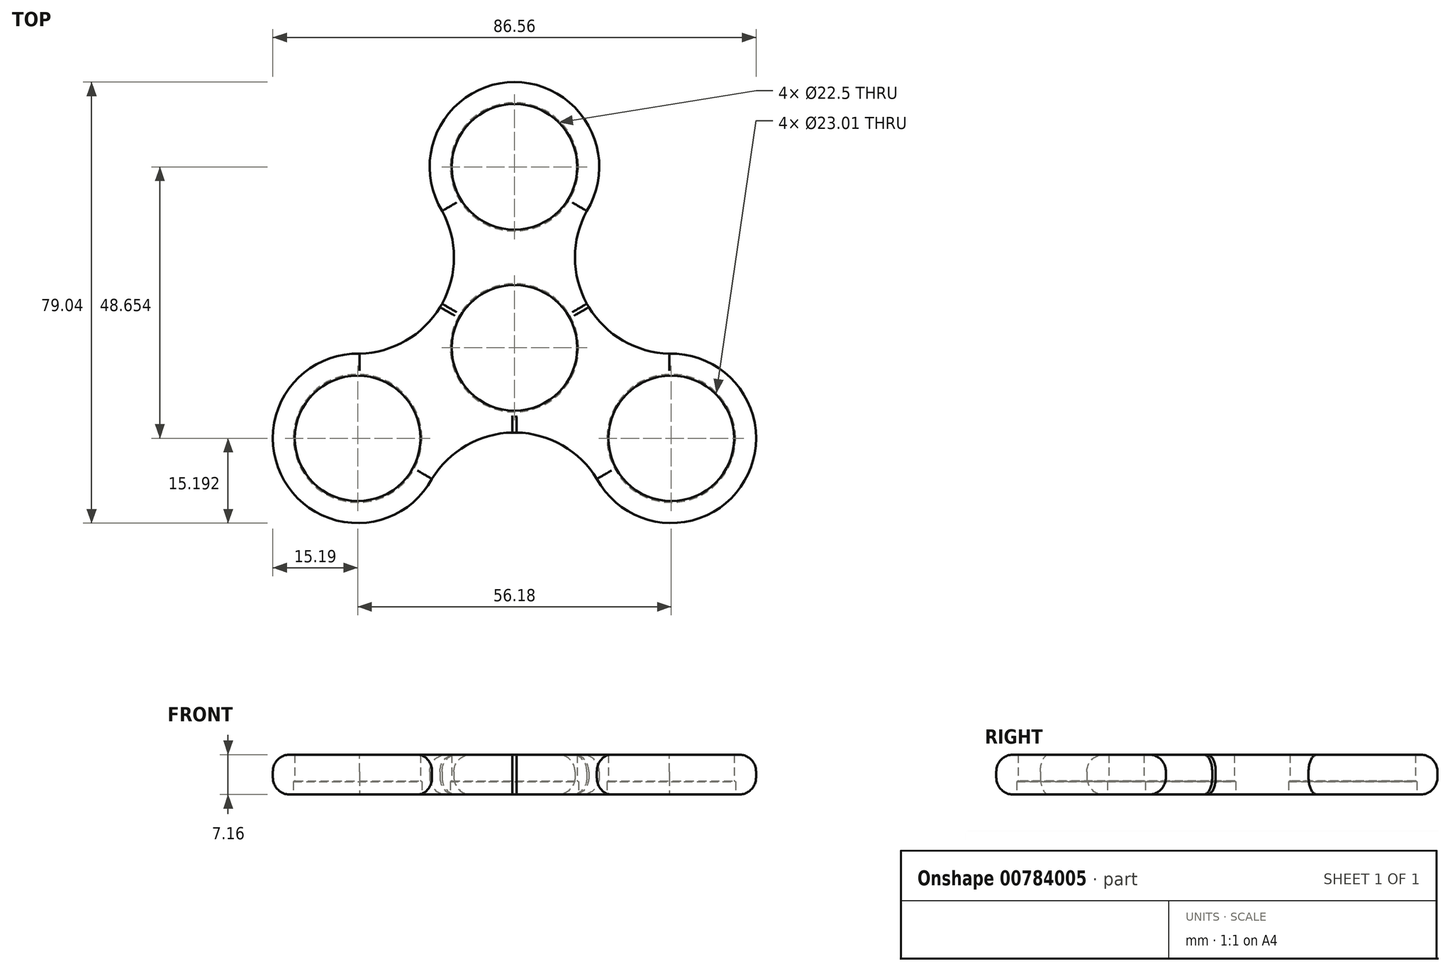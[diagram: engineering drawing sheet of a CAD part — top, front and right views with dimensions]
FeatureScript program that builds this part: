
annotation { "Feature Type Name" : "Feature", "Feature Type Description" : "" }
export const myFeature = defineFeature(function(context is Context, id is Id, definition is map)
    precondition{}
    {
        {
            var Q0;
            Q0=qCreatedBy(makeId("Top.planeOp"),FACE);
            var sketch = newSketch(context, id + "F0", { "sketchPlane" : qUnion([Q0])});
            skCircle(sketch, "E0", {"center": v(0, 0) * mm, "radius": 11.25 * mm});
            skCircle(sketch, "E1", {"center": v(0, 0) * mm, "radius": 15.19 * mm});
            skCircle(sketch, "E2.1.0", {"center": v(0, 32.44) * mm, "radius": 15.19 * mm});
            skCircle(sketch, "E2.1.1", {"center": v(0, 32.44) * mm, "radius": 11.25 * mm});
            skLineSegment(sketch, "E3", {"start": v(0, 0) * mm, "end": v(0, 32.44) * mm, "construction": true});
            skLineSegment(sketch, "E4", {"start": v(0, 32.44) * mm, "end": v(28.1, 16.22) * mm, "construction": true});
            skArc(sketch, "E5", {"start": v(13.33, 7.28) * mm, "mid": v(10.84, 16.04) * mm, "end": v(13.15, 24.85) * mm});
            skArc(sketch, "E6.MirrorCS", {"start": v(-13.33, 7.28) * mm, "mid": v(-10.84, 16.04) * mm, "end": v(-13.15, 24.85) * mm});
            skCircle(sketch, "E7.1.1", {"center": v(-28.1, -16.22) * mm, "radius": 11.25 * mm});
            skCircle(sketch, "E7.1.2", {"center": v(-28.1, -16.22) * mm, "radius": 15.19 * mm});
            skArc(sketch, "E7.1.3", {"start": v(0.36, -15.18) * mm, "mid": v(-8.47, -17.4) * mm, "end": v(-14.94, -23.8) * mm});
            skArc(sketch, "E7.1.4", {"start": v(-12.97, 7.9) * mm, "mid": v(-19.3, 1.37) * mm, "end": v(-28.1, -1.04) * mm});
            skCircle(sketch, "E7.2.1", {"center": v(28.1, -16.22) * mm, "radius": 11.25 * mm});
            skCircle(sketch, "E7.2.2", {"center": v(28.1, -16.22) * mm, "radius": 15.19 * mm});
            skArc(sketch, "E7.2.3", {"start": v(12.97, 7.9) * mm, "mid": v(19.3, 1.37) * mm, "end": v(28.1, -1.04) * mm});
            skArc(sketch, "E7.2.4", {"start": v(-0.36, -15.18) * mm, "mid": v(8.47, -17.4) * mm, "end": v(14.94, -23.8) * mm});
            skSolve(sketch);
        }
        {
            var Q0;
            Q0 = qSketchRegion(id + "F0", true);
            extrude(context, id + "F1", {"entities" : qUnion([Q0]), "depth" : 7.16 * mm, "offsetDistance" : 25.4 * mm});
        }
        {
            var Q0;
            Q0=sQuery(id+"F0.wireOp",VERTEX,"E2.1.2.start");
            var Q1;
            Q1=sQuery(id+"F0.wireOp",VERTEX,"E0.center");
            var Q2;
            Q2=sQuery(id+"F0.wireOp",VERTEX,"DuPa364O-TqXS-B9n7-HQNF-Pfb0DS6MvXj8.end");
            var Q3;
            Q3=sQuery(id+"F0.wireOp",VERTEX,"E2.2.2.start");
            var Q4;
            Q4=makeQuery(id+"F1.opExtrude","SWEPT_BODY",BODY,{"disambiguationData":[OSD([sQuery(id+"F0.wireOp",EDGE,"E0"),sQuery(id+"F0.wireOp",EDGE,"49040aab-aefb-4229-aee8-8bc108439dca"),sQuery(id+"F0.wireOp",EDGE,"cf4a4477-fab2-41f1-a485-c14e34cd1196"),sQuery(id+"F0.wireOp",EDGE,"E2.1.0"),sQuery(id+"F0.wireOp",EDGE,"E2.1.1"),sQuery(id+"F0.wireOp",EDGE,"E2.2.0"),sQuery(id+"F0.wireOp",EDGE,"E2.2.1"),sQuery(id+"F0.wireOp",EDGE,"L5vnPDiK-83xg-WwNy-e8JY-2QZKI3Z6EqPW"),sQuery(id+"F0.wireOp",EDGE,"0c184fe2-091d-4b9e-b4e7-c48332455db4.1.0"),sQuery(id+"F0.wireOp",EDGE,"0c184fe2-091d-4b9e-b4e7-c48332455db4.2.0")])]});
            hole(context, id + "F2", {"style" : HoleStyle.SIMPLE, "endStyle" : HoleEndStyle.BLIND, "oppositeDirection" : true, "holeDiameter" : 23.01 * mm, "majorDiameter" : 6.35 * mm, "holeDepth" : 2.3 * mm, "isTappedThrough" : true, "tappedDepth" : 12.7 * mm, "tapClearance" : 3, "locations" : qUnion([Q0, Q1, Q2, Q3]), "scope" : qUnion([Q4])});
        }
        {
            var Q0;
            Q0=sQuery(id+"F0.wireOp",VERTEX,"E7.1.1.center");
            var Q1;
            Q1=sQuery(id+"F0.wireOp",VERTEX,"E7.2.1.center");
            var Q2;
            Q2=sQuery(id+"F0.wireOp",VERTEX,"E3.end");
            var Q3;
            Q3=makeQuery(id+"F1.opExtrude","SWEPT_BODY",BODY,{"disambiguationData":[OSD([sQuery(id+"F0.wireOp",EDGE,"E0"),sQuery(id+"F0.wireOp",EDGE,"E1"),sQuery(id+"F0.wireOp",EDGE,"E2.1.0"),sQuery(id+"F0.wireOp",EDGE,"E2.1.1"),sQuery(id+"F0.wireOp",EDGE,"E5"),sQuery(id+"F0.wireOp",EDGE,"E6.MirrorCS"),sQuery(id+"F0.wireOp",EDGE,"E7.1.1"),sQuery(id+"F0.wireOp",EDGE,"E7.1.2"),sQuery(id+"F0.wireOp",EDGE,"E7.1.3"),sQuery(id+"F0.wireOp",EDGE,"E7.1.4"),sQuery(id+"F0.wireOp",EDGE,"E7.2.1"),sQuery(id+"F0.wireOp",EDGE,"E7.2.2"),sQuery(id+"F0.wireOp",EDGE,"E7.2.3"),sQuery(id+"F0.wireOp",EDGE,"E7.2.4")])]});
            hole(context, id + "F3", {"style" : HoleStyle.SIMPLE, "endStyle" : HoleEndStyle.BLIND, "oppositeDirection" : true, "holeDiameter" : 23.01 * mm, "majorDiameter" : 6.35 * mm, "holeDepth" : 2.3 * mm, "isTappedThrough" : true, "tappedDepth" : 12.7 * mm, "tapClearance" : 3, "locations" : qUnion([Q0, Q1, Q2]), "scope" : qUnion([Q3])});
        }
        {
            var Q0;
            Q0=makeQuery(id+"F1.opExtrude","CAP_EDGE",EDGE,{"disambiguationData":[OSD([sQuery(id+"F0.wireOp",EDGE,"E7.1.4")])],"isStart":false});
            var Q1;
            Q1=makeQuery(id+"F1.opExtrude","CAP_EDGE",EDGE,{"disambiguationData":[OSD([sQuery(id+"F0.wireOp",EDGE,"E7.1.2")])],"isStart":false});
            var Q2;
            Q2=makeQuery(id+"F1.opExtrude","CAP_EDGE",EDGE,{"disambiguationData":[OSD([sQuery(id+"F0.wireOp",EDGE,"E7.1.3")])],"isStart":false});
            var Q3;
            Q3=makeQuery(id+"F1.opExtrude","CAP_EDGE",EDGE,{"disambiguationData":[OSD([sQuery(id+"F0.wireOp",EDGE,"E7.2.4")])],"isStart":false});
            var Q4;
            Q4=makeQuery(id+"F1.opExtrude","CAP_EDGE",EDGE,{"disambiguationData":[OSD([sQuery(id+"F0.wireOp",EDGE,"E7.2.2")])],"isStart":false});
            var Q5;
            Q5=makeQuery(id+"F1.opExtrude","CAP_EDGE",EDGE,{"disambiguationData":[OSD([sQuery(id+"F0.wireOp",EDGE,"E7.2.3")])],"isStart":false});
            var Q6;
            Q6=makeQuery(id+"F1.opExtrude","CAP_EDGE",EDGE,{"disambiguationData":[OSD([sQuery(id+"F0.wireOp",EDGE,"E5")])],"isStart":false});
            var Q7;
            Q7=makeQuery(id+"F1.opExtrude","CAP_EDGE",EDGE,{"disambiguationData":[OSD([sQuery(id+"F0.wireOp",EDGE,"E2.1.0")])],"isStart":false});
            var Q8;
            Q8=makeQuery(id+"F1.opExtrude","CAP_EDGE",EDGE,{"disambiguationData":[OSD([sQuery(id+"F0.wireOp",EDGE,"E6.MirrorCS")])],"isStart":false});
            var Q9;
            {var subQ0=sQuery(id+"F0.wireOp",EDGE,"E7.1.4");var subQ1=sQuery(id+"F0.wireOp",EDGE,"E1");Q9=makeQuery(id+"F1.opExtrude","CAP_EDGE",EDGE,{"disambiguationData":[OSD([subQ1]),TDD([makeQuery(id+"F0.imprint","IMPRINT",EDGE,{"disambiguationData":[TD([[makeQuery(id+"F0.imprint","INTERSECT",VERTEX,{"derivedFrom":[subQ1,subQ0]}),1.0]])],"derivedFrom":subQ1})])],"isStart":false});}
            var Q10;
            {var subQ0=sQuery(id+"F0.wireOp",EDGE,"E7.2.4");var subQ1=sQuery(id+"F0.wireOp",EDGE,"E1");Q10=makeQuery(id+"F1.opExtrude","CAP_EDGE",EDGE,{"disambiguationData":[OSD([subQ1]),TDD([makeQuery(id+"F0.imprint","IMPRINT",EDGE,{"disambiguationData":[TD([[makeQuery(id+"F0.imprint","INTERSECT",VERTEX,{"derivedFrom":[subQ1,subQ0]}),1.0]])],"derivedFrom":subQ1})])],"isStart":false});}
            var Q11;
            {var subQ0=sQuery(id+"F0.wireOp",EDGE,"E7.2.3");var subQ1=sQuery(id+"F0.wireOp",EDGE,"E1");Q11=makeQuery(id+"F1.opExtrude","CAP_EDGE",EDGE,{"disambiguationData":[OSD([subQ1]),TDD([makeQuery(id+"F0.imprint","IMPRINT",EDGE,{"disambiguationData":[TD([[makeQuery(id+"F0.imprint","INTERSECT",VERTEX,{"derivedFrom":[subQ1,subQ0]}),-1.0]])],"derivedFrom":subQ1})])],"isStart":false});}
            fillet(context, id + "F4", {"entities" : qUnion([Q0, Q1, Q2, Q3, Q4, Q5, Q6, Q7, Q8, Q9, Q10, Q11]), "radius" : 3.05 * mm, "tangentPropagation" : true, "allowEdgeOverflow" : false});
        }
        {
            var Q0;
            Q0=makeQuery(id+"F1.opExtrude","CAP_EDGE",EDGE,{"disambiguationData":[OSD([sQuery(id+"F0.wireOp",EDGE,"E6.MirrorCS")])],"isStart":true});
            var Q1;
            Q1=makeQuery(id+"F1.opExtrude","CAP_EDGE",EDGE,{"disambiguationData":[OSD([sQuery(id+"F0.wireOp",EDGE,"E2.1.0")])],"isStart":true});
            var Q2;
            Q2=makeQuery(id+"F1.opExtrude","CAP_EDGE",EDGE,{"disambiguationData":[OSD([sQuery(id+"F0.wireOp",EDGE,"E5")])],"isStart":true});
            var Q3;
            Q3=makeQuery(id+"F1.opExtrude","CAP_EDGE",EDGE,{"disambiguationData":[OSD([sQuery(id+"F0.wireOp",EDGE,"E7.2.3")])],"isStart":true});
            var Q4;
            Q4=makeQuery(id+"F1.opExtrude","CAP_EDGE",EDGE,{"disambiguationData":[OSD([sQuery(id+"F0.wireOp",EDGE,"E7.2.2")])],"isStart":true});
            var Q5;
            Q5=makeQuery(id+"F1.opExtrude","CAP_EDGE",EDGE,{"disambiguationData":[OSD([sQuery(id+"F0.wireOp",EDGE,"E7.2.4")])],"isStart":true});
            var Q6;
            Q6=makeQuery(id+"F1.opExtrude","CAP_EDGE",EDGE,{"disambiguationData":[OSD([sQuery(id+"F0.wireOp",EDGE,"E7.1.3")])],"isStart":true});
            var Q7;
            Q7=makeQuery(id+"F1.opExtrude","CAP_EDGE",EDGE,{"disambiguationData":[OSD([sQuery(id+"F0.wireOp",EDGE,"E7.1.2")])],"isStart":true});
            var Q8;
            Q8=makeQuery(id+"F1.opExtrude","CAP_EDGE",EDGE,{"disambiguationData":[OSD([sQuery(id+"F0.wireOp",EDGE,"E7.1.4")])],"isStart":true});
            var Q9;
            {var subQ0=sQuery(id+"F0.wireOp",EDGE,"E7.1.4");var subQ1=sQuery(id+"F0.wireOp",EDGE,"E1");Q9=makeQuery(id+"F1.opExtrude","CAP_EDGE",EDGE,{"disambiguationData":[OSD([subQ1]),TDD([makeQuery(id+"F0.imprint","IMPRINT",EDGE,{"disambiguationData":[TD([[makeQuery(id+"F0.imprint","INTERSECT",VERTEX,{"derivedFrom":[subQ1,subQ0]}),1.0]])],"derivedFrom":subQ1})])],"isStart":true});}
            var Q10;
            {var subQ0=sQuery(id+"F0.wireOp",EDGE,"E7.2.4");var subQ1=sQuery(id+"F0.wireOp",EDGE,"E1");Q10=makeQuery(id+"F1.opExtrude","CAP_EDGE",EDGE,{"disambiguationData":[OSD([subQ1]),TDD([makeQuery(id+"F0.imprint","IMPRINT",EDGE,{"disambiguationData":[TD([[makeQuery(id+"F0.imprint","INTERSECT",VERTEX,{"derivedFrom":[subQ1,subQ0]}),1.0]])],"derivedFrom":subQ1})])],"isStart":true});}
            var Q11;
            {var subQ0=sQuery(id+"F0.wireOp",EDGE,"E7.2.3");var subQ1=sQuery(id+"F0.wireOp",EDGE,"E1");Q11=makeQuery(id+"F1.opExtrude","CAP_EDGE",EDGE,{"disambiguationData":[OSD([subQ1]),TDD([makeQuery(id+"F0.imprint","IMPRINT",EDGE,{"disambiguationData":[TD([[makeQuery(id+"F0.imprint","INTERSECT",VERTEX,{"derivedFrom":[subQ1,subQ0]}),-1.0]])],"derivedFrom":subQ1})])],"isStart":true});}
            fillet(context, id + "F5", {"entities" : qUnion([Q0, Q1, Q2, Q3, Q4, Q5, Q6, Q7, Q8, Q9, Q10, Q11]), "radius" : 3.05 * mm, "tangentPropagation" : true, "allowEdgeOverflow" : false});
        }
    });
